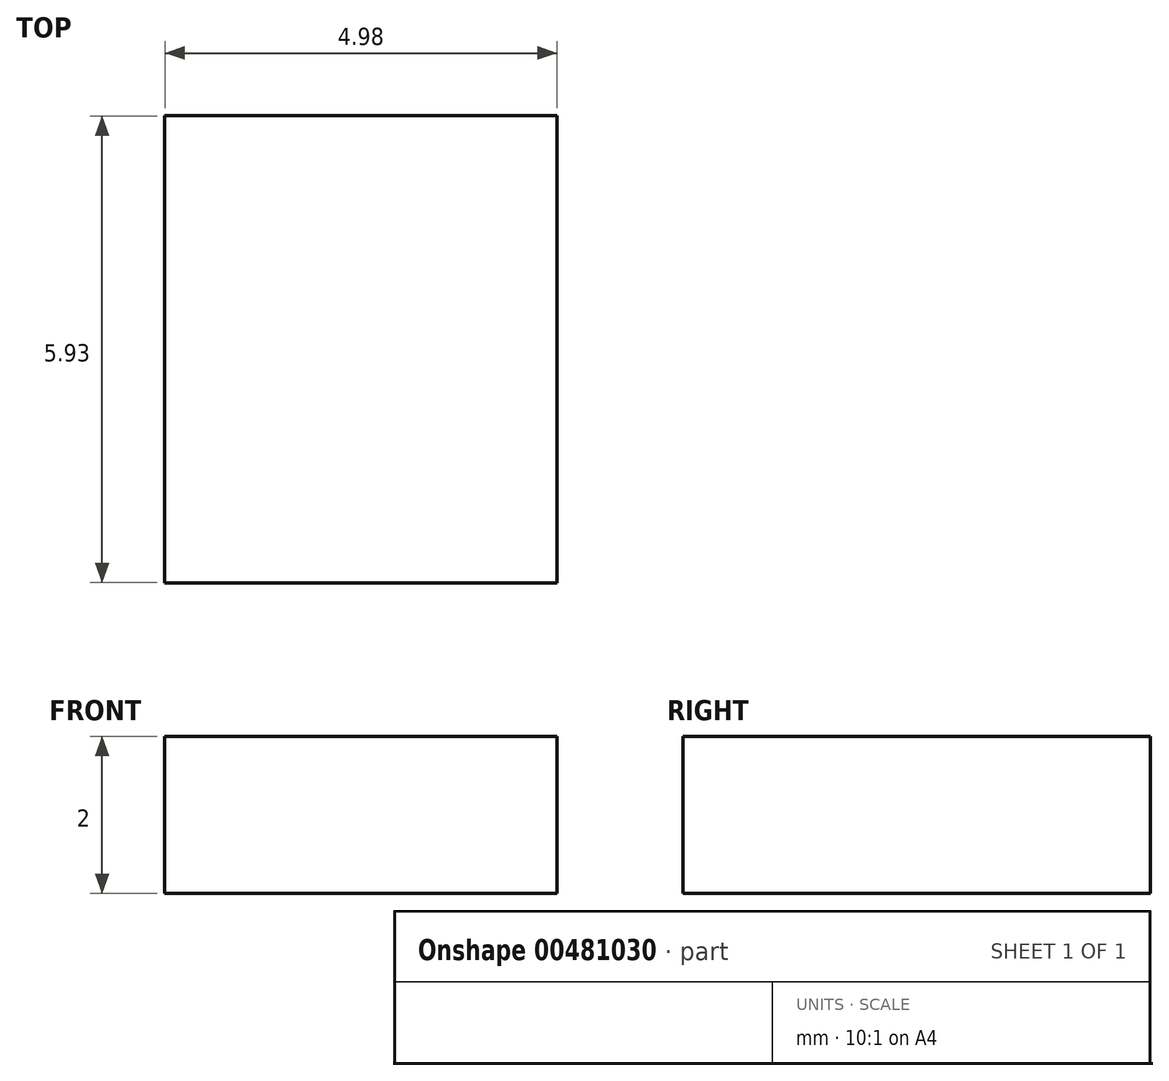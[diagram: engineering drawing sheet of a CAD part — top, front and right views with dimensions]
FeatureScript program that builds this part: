
annotation { "Feature Type Name" : "Feature", "Feature Type Description" : "" }
export const myFeature = defineFeature(function(context is Context, id is Id, definition is map)
    precondition{}
    {
        {
            var Q0;
            Q0=qCreatedBy(makeId("Top.planeOp"),FACE);
            var sketch = newSketch(context, id + "F0", { "sketchPlane" : qUnion([Q0])});
            skLineSegment(sketch, "E0.bottom", {"start": v(-2.37, 3) * mm, "end": v(2.61, 3) * mm});
            skLineSegment(sketch, "E0.top", {"start": v(-2.37, -2.94) * mm, "end": v(2.61, -2.94) * mm});
            skLineSegment(sketch, "E0.left", {"start": v(-2.37, 3) * mm, "end": v(-2.37, -2.94) * mm});
            skLineSegment(sketch, "E0.right", {"start": v(2.61, 3) * mm, "end": v(2.61, -2.94) * mm});
            skSolve(sketch);
        }
        {
            var Q0;
            Q0=makeQuery(id+"F0.imprint","IMPRINT",FACE,{"disambiguationData":[TD([[makeQuery(id+"F0.imprint","IMPRINT",EDGE,{"derivedFrom":sQuery(id+"F0.wireOp",EDGE,"E0.bottom")}),-1.0]])]});
            extrude(context, id + "F1", {"entities" : qUnion([Q0]), "depth" : 2 * mm});
        }
    });
